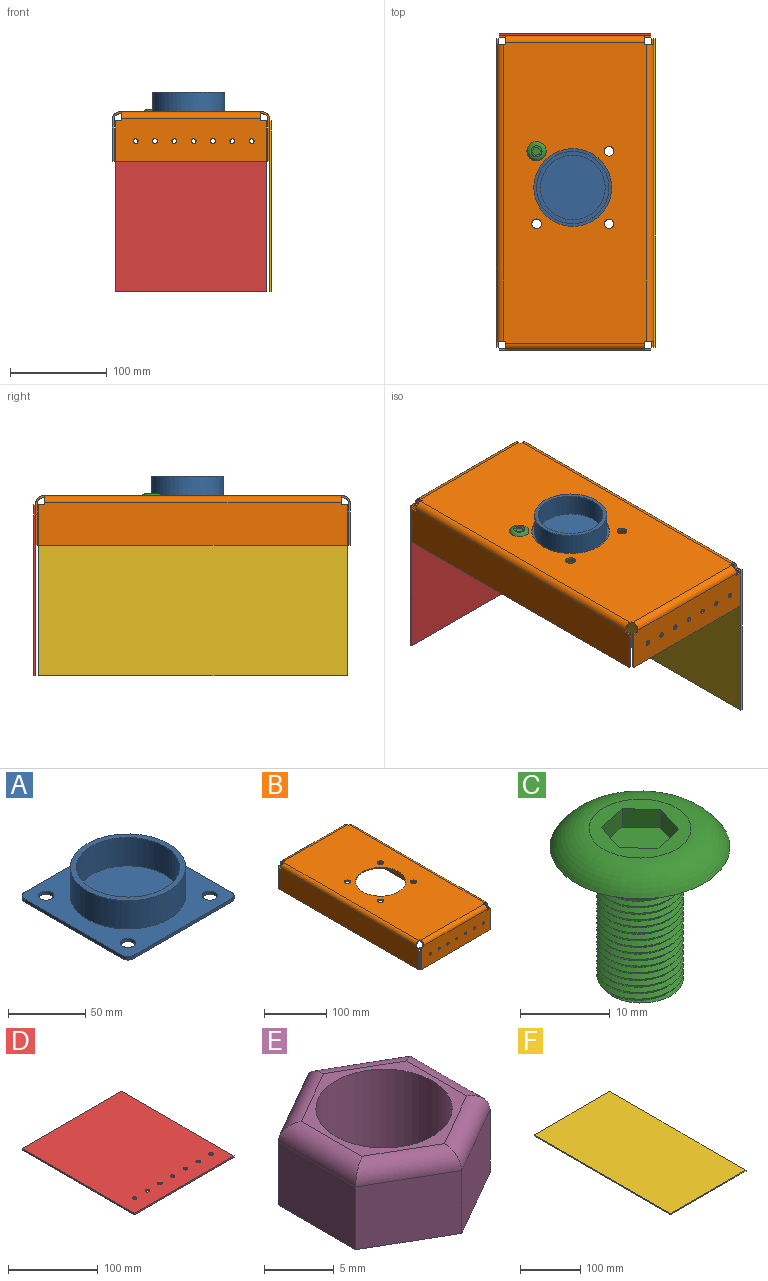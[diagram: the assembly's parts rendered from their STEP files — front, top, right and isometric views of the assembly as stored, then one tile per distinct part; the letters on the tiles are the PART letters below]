
ASSEMBLY  parts=6 mates=5
PART A: 18 faces, bbox 100x100x25 mm
  f0: plane 90x2.5mm, normal (0,1,0), area 225mm2, adj f1,f7,f8,f9
  f1: cylinder r=5mm len=5mm, axis (0,0,-1), area 19.6mm2, adj f0,f2,f8,f9
  f2: plane 90x2.5mm, normal (-1,0,0), area 225mm2, adj f1,f3,f8,f9
  f3: cylinder r=5mm len=5mm, axis (0,0,-1), area 19.6mm2, adj f2,f4,f8,f9
  f4: plane 90x2.5mm, normal (0,-1,0), area 225mm2, adj f3,f5,f8,f9
  f5: cylinder r=5mm len=5mm, axis (0,0,-1), area 19.6mm2, adj f4,f6,f8,f9
  f6: plane 90x2.5mm, normal (1,0,0), area 225mm2, adj f5,f7,f8,f9
  f7: cylinder r=5mm len=5mm, axis (0,0,-1), area 19.6mm2, adj f0,f6,f8,f9
  f8: plane 100x100mm, normal (0,0,1), area 5279.1mm2, adj f0,f1,f2,f3,f4,f5,f6,f7
  f9: plane 100x100mm, normal (0,0,-1), area 9664.4mm2, adj f0,f1,f2,f3,f4,f5,f6,f7
  f10: cylinder r=5mm len=10mm, axis (0,0,-1), area 78.5mm2, adj f8,f9
  f11: cylinder r=5mm len=10mm, axis (0,0,-1), area 78.5mm2, adj f8,f9
  f12: cylinder r=5mm len=10mm, axis (0,0,-1), area 78.5mm2, adj f8,f9
  f13: cylinder r=5mm len=10mm, axis (0,0,-1), area 78.5mm2, adj f8,f9
  f14: cylinder r=33.4mm len=66.8mm, axis (0,0,-1), area 4721.7mm2, adj f16,f17
  f15: cylinder r=37.36mm len=74.72mm, axis (0,0,-1), area 5281.8mm2, adj f8,f16
  f16: plane 74.72x74.72mm, normal (0,0,1), area 880.8mm2, adj f14,f15
  f17: plane 66.8x66.8mm, normal (0,0,1), area 3504.5mm2, adj f14
PART B: 81 faces, bbox 162.5x325x51 mm
  f0: plane 41.68x2mm, normal (-1,0,0), area 83.4mm2, adj f2,f3,f4,f5
  f1: plane 41.68x2mm, normal (1,0,0), area 83.4mm2, adj f2,f3,f4,f8
  f2: plane 156.52x44mm, normal (0,-1,0), area 6720.4mm2, adj f0,f1,f4,f5,f6,f7,f8,f65
  f3: plane 156.52x44mm, normal (0,1,0), area 6720.4mm2, adj f0,f1,f4,f5,f6,f7,f8,f66
  f4: plane 156.52x2mm, normal (0,0,-1), area 313mm2, adj f0,f1,f2,f3
  f5: plane 6.32x2mm, normal (0,0,1), area 12.6mm2, adj f0,f2,f3,f6
  f6: plane 2.32x2mm, normal (-1,0,0), area 4.6mm2, adj f2,f3,f5,f64
  f7: plane 2.32x2mm, normal (1,0,0), area 4.6mm2, adj f2,f3,f8,f63
  f8: plane 6.32x2mm, normal (0,0,1), area 12.6mm2, adj f1,f2,f3,f7
  f9: plane 311.05x148.52mm, normal (0,0,1), area 40789.9mm2, adj f11,f12,f13,f14,f15,f16,f17,f18
  f10: plane 311.05x148.52mm, normal (0,0,-1), area 40789.9mm2, adj f11,f12,f13,f14,f15,f16,f17,f18
  f11: cylinder r=4.98mm len=9.95mm, axis (0,0,1), area 62.5mm2, adj f9,f10
  f12: cylinder r=4.86mm len=9.73mm, axis (0,0,1), area 61.1mm2, adj f9,f10
  f13: cylinder r=4.98mm len=9.96mm, axis (0,0,1), area 62.6mm2, adj f9,f10
  f14: cylinder r=4.86mm len=9.72mm, axis (0,0,1), area 61.1mm2, adj f9,f10
  f15: cylinder r=40.22mm len=80.44mm, axis (0,0,1), area 505.4mm2, adj f9,f10
  f16: plane 2.32x2mm, normal (-1,0,0), area 4.6mm2, adj f9,f10,f17,f34
  f17: plane 2.32x2mm, normal (0,1,0), area 4.6mm2, adj f9,f10,f16,f46
  f18: plane 2.32x2mm, normal (0,-1,0), area 4.6mm2, adj f9,f10,f19,f47
  f19: plane 2.32x2mm, normal (-1,0,0), area 4.6mm2, adj f9,f10,f18,f64
  f20: plane 2.32x2mm, normal (1,0,0), area 4.6mm2, adj f9,f10,f21,f63
  f21: plane 2.32x2mm, normal (0,-1,0), area 4.6mm2, adj f9,f10,f20,f60
  f22: plane 2.32x2mm, normal (0,1,0), area 4.6mm2, adj f9,f10,f23,f59
  f23: plane 2.32x2mm, normal (1,0,0), area 4.6mm2, adj f9,f10,f22,f33
  f24: plane 41.68x2mm, normal (1,0,0), area 83.4mm2, adj f26,f27,f28,f29
  f25: plane 41.68x2mm, normal (-1,0,0), area 83.4mm2, adj f26,f27,f28,f32
  f26: plane 156.52x44mm, normal (0,1,0), area 6720.4mm2, adj f24,f25,f28,f29,f30,f31,f32,f35
  f27: plane 156.52x44mm, normal (0,-1,0), area 6720.4mm2, adj f24,f25,f28,f29,f30,f31,f32,f36
  f28: plane 156.52x2mm, normal (0,0,-1), area 313mm2, adj f24,f25,f26,f27
  f29: plane 6.32x2mm, normal (0,0,1), area 12.6mm2, adj f24,f26,f27,f30
  f30: plane 2.32x2mm, normal (1,0,0), area 4.6mm2, adj f26,f27,f29,f33
  f31: plane 2.32x2mm, normal (-1,0,0), area 4.6mm2, adj f26,f27,f32,f34
  f32: plane 6.32x2mm, normal (0,0,1), area 12.6mm2, adj f25,f26,f27,f31
  f33: plane 7x7mm, normal (1,0,0), area 18.8mm2, adj f23,f30,f35,f36
  f34: plane 7x7mm, normal (-1,0,0), area 18.8mm2, adj f16,f31,f35,f36
  f35: cylinder r=7mm len=143.89mm, axis (1,0,0), area 1582.2mm2, adj f9,f26,f33,f34
  f36: cylinder r=5mm len=143.89mm, axis (1,0,0), area 1130.1mm2, adj f10,f27,f33,f34
  f37: plane 41.68x2mm, normal (0,1,0), area 83.4mm2, adj f39,f40,f41,f42
  f38: plane 41.68x2mm, normal (0,-1,0), area 83.4mm2, adj f39,f40,f41,f45
  f39: plane 319.05x44mm, normal (-1,0,0), area 14008.8mm2, adj f37,f38,f41,f42,f43,f44,f45,f48
  f40: plane 319.05x44mm, normal (1,0,0), area 14008.8mm2, adj f37,f38,f41,f42,f43,f44,f45,f49
  f41: plane 319.05x2mm, normal (0,0,-1), area 638.1mm2, adj f37,f38,f39,f40
  f42: plane 6.32x2mm, normal (0,0,1), area 12.6mm2, adj f37,f39,f40,f43
  f43: plane 2.32x2mm, normal (0,1,0), area 4.6mm2, adj f39,f40,f42,f46
  f44: plane 2.32x2mm, normal (0,-1,0), area 4.6mm2, adj f39,f40,f45,f47
  f45: plane 6.32x2mm, normal (0,0,1), area 12.6mm2, adj f38,f39,f40,f44
  f46: plane 7x7mm, normal (0,1,0), area 18.8mm2, adj f17,f43,f48,f49
  f47: plane 7x7mm, normal (0,-1,0), area 18.8mm2, adj f18,f44,f48,f49
  f48: cylinder r=7mm len=306.41mm, axis (0,1,0), area 3369.2mm2, adj f9,f39,f46,f47
  f49: cylinder r=5mm len=306.41mm, axis (0,1,0), area 2406.6mm2, adj f10,f40,f46,f47
  f50: plane 41.68x2mm, normal (0,-1,0), area 83.4mm2, adj f52,f53,f54,f55
  f51: plane 41.68x2mm, normal (0,1,0), area 83.4mm2, adj f52,f53,f54,f58
  f52: plane 319.05x44mm, normal (1,0,0), area 14008.8mm2, adj f50,f51,f54,f55,f56,f57,f58,f61
  f53: plane 319.05x44mm, normal (-1,0,0), area 14008.8mm2, adj f50,f51,f54,f55,f56,f57,f58,f62
  f54: plane 319.05x2mm, normal (0,0,-1), area 638.1mm2, adj f50,f51,f52,f53
  f55: plane 6.32x2mm, normal (0,0,1), area 12.6mm2, adj f50,f52,f53,f56
  f56: plane 2.32x2mm, normal (0,-1,0), area 4.6mm2, adj f52,f53,f55,f60
  f57: plane 2.32x2mm, normal (0,1,0), area 4.6mm2, adj f52,f53,f58,f59
  f58: plane 6.32x2mm, normal (0,0,1), area 12.6mm2, adj f51,f52,f53,f57
  f59: plane 7x7mm, normal (0,1,0), area 18.8mm2, adj f22,f57,f61,f62
  f60: plane 7x7mm, normal (0,-1,0), area 18.8mm2, adj f21,f56,f61,f62
  f61: cylinder r=7mm len=306.41mm, axis (0,1,0), area 3369.2mm2, adj f9,f52,f59,f60
  f62: cylinder r=5mm len=306.41mm, axis (0,1,0), area 2406.6mm2, adj f10,f53,f59,f60
  f63: plane 7x7mm, normal (1,0,0), area 18.8mm2, adj f7,f20,f65,f66
  f64: plane 7x7mm, normal (-1,0,0), area 18.8mm2, adj f6,f19,f65,f66
  f65: cylinder r=7mm len=143.89mm, axis (1,0,0), area 1582.2mm2, adj f2,f9,f63,f64
  f66: cylinder r=5mm len=143.89mm, axis (1,0,0), area 1130.1mm2, adj f3,f10,f63,f64
  f67: cylinder r=2.5mm len=5mm, axis (0,-1,0), area 31.4mm2, adj f26,f27
  f68: cylinder r=2.5mm len=5mm, axis (0,-1,0), area 31.4mm2, adj f2,f3
  f69: cylinder r=2.5mm len=5mm, axis (0,-1,0), area 31.4mm2, adj f26,f27
  f70: cylinder r=2.5mm len=5mm, axis (0,-1,0), area 31.4mm2, adj f2,f3
  f71: cylinder r=2.5mm len=5mm, axis (0,-1,0), area 31.4mm2, adj f26,f27
  f72: cylinder r=2.5mm len=5mm, axis (0,-1,0), area 31.4mm2, adj f2,f3
  f73: cylinder r=2.5mm len=5mm, axis (0,-1,0), area 31.4mm2, adj f26,f27
  f74: cylinder r=2.5mm len=5mm, axis (0,-1,0), area 31.4mm2, adj f2,f3
  f75: cylinder r=2.5mm len=5mm, axis (0,-1,0), area 31.4mm2, adj f26,f27
  f76: cylinder r=2.5mm len=5mm, axis (0,-1,0), area 31.4mm2, adj f2,f3
  f77: cylinder r=2.5mm len=5mm, axis (0,-1,0), area 31.4mm2, adj f26,f27
  f78: cylinder r=2.5mm len=5mm, axis (0,-1,0), area 31.4mm2, adj f2,f3
  f79: cylinder r=2.5mm len=5mm, axis (0,-1,0), area 31.4mm2, adj f26,f27
  f80: cylinder r=2.5mm len=5mm, axis (0,-1,0), area 31.4mm2, adj f2,f3
PART C: 16 faces, bbox 23.5x23.5x21.4 mm
  f0: plane 11.34x11.34mm, normal (0,0,1), area 52.4mm2, adj f3,f9,f10,f11,f12,f13,f14
  f1: cylinder r=5mm len=10mm, axis (0,0,1), area 116.7mm2, adj f2,f6,f7
  f2: plane 20x20mm, normal (0,0,-1), area 235.6mm2, adj f1,f3
  f3: torus R=5.67mm, axis (0,0,-1), area 265.1mm2, adj f0,f2
  f4: bspline ~15.01x11.11mm, area 281.6mm2, adj f5,f6,f7,f8
  f5: bspline ~14.54x11.11mm, area 263mm2, adj f4,f6,f8
  f6: plane 1.12x0.59mm, normal (0,-1,0), area 0.4mm2, adj f1,f4,f5,f7
  f7: bspline ~11.55x10mm, area 9mm2, adj f1,f4,f6
  f8: plane 9.64x9.63mm, normal (0,0,-1), area 66.8mm2, adj f4,f5
  f9: plane 4.22x2.5mm, normal (-0.22,0.98,0), area 10.8mm2, adj f0,f10,f14,f15
  f10: plane 4.12x2.5mm, normal (-0.95,0.3,0), area 10.8mm2, adj f0,f9,f11,f15
  f11: plane 3.19x2.92mm, normal (-0.74,-0.67,0), area 10.8mm2, adj f0,f10,f12,f15
  f12: plane 4.22x2.5mm, normal (0.22,-0.98,0), area 10.8mm2, adj f0,f11,f13,f15
  f13: plane 4.12x2.5mm, normal (0.95,-0.3,0), area 10.8mm2, adj f0,f12,f14,f15
  f14: plane 3.19x2.92mm, normal (0.74,0.67,0), area 10.8mm2, adj f0,f9,f13,f15
  f15: plane 8.45x8.25mm, normal (0,0,1), area 48.6mm2, adj f9,f10,f11,f12,f13,f14
PART D: 13 faces, bbox 156.5x176.8x2 mm
  f0: plane 156.52x2mm, normal (0,1,0), area 313mm2, adj f1,f10,f11,f12
  f1: plane 176.78x2mm, normal (1,0,0), area 353.6mm2, adj f0,f2,f11,f12
  f2: plane 156.52x2mm, normal (0,-1,0), area 313mm2, adj f1,f10,f11,f12
  f3: cylinder r=2.5mm len=5mm, axis (0,0,1), area 31.4mm2, adj f11,f12
  f4: cylinder r=2.5mm len=5mm, axis (0,0,1), area 31.4mm2, adj f11,f12
  f5: cylinder r=2.5mm len=5mm, axis (0,0,1), area 31.4mm2, adj f11,f12
  f6: cylinder r=2.5mm len=5mm, axis (0,0,1), area 31.4mm2, adj f11,f12
  f7: cylinder r=2.5mm len=5mm, axis (0,0,1), area 31.4mm2, adj f11,f12
  f8: cylinder r=2.5mm len=5mm, axis (0,0,1), area 31.4mm2, adj f11,f12
  f9: cylinder r=2.5mm len=5mm, axis (0,0,1), area 31.4mm2, adj f11,f12
  f10: plane 176.78x2mm, normal (-1,0,0), area 353.6mm2, adj f0,f2,f11,f12
  f11: plane 176.78x156.52mm, normal (0,0,-1), area 27533.2mm2, adj f0,f1,f2,f3,f4,f5,f6,f7
  f12: plane 176.78x156.52mm, normal (0,0,1), area 27533.2mm2, adj f0,f1,f2,f3,f4,f5,f6,f7
PART E: 15 faces, bbox 13.6x15.7x7 mm
  f0: plane 6.8x5.5mm, normal (0.5,0.87,0), area 43.2mm2, adj f1,f5,f8,f12
  f1: plane 6.8x5.5mm, normal (-0.5,0.87,0), area 43.2mm2, adj f0,f2,f8,f10
  f2: plane 7.85x5.5mm, normal (-1,0,0), area 43.2mm2, adj f1,f3,f8,f9
  f3: plane 6.8x5.5mm, normal (-0.5,-0.87,0), area 43.2mm2, adj f2,f4,f8,f11
  f4: plane 6.8x5.5mm, normal (0.5,-0.87,0), area 43.2mm2, adj f3,f5,f8,f13
  f5: plane 7.85x5.5mm, normal (1,0,0), area 43.2mm2, adj f0,f4,f8,f14
  f6: cylinder r=4.87mm len=9.75mm, axis (0,0,-1), area 214.4mm2, adj f7,f8
  f7: plane 12.23x10.59mm, normal (0,0,1), area 22.5mm2, adj f6,f9,f10,f11,f12,f13,f14
  f8: plane 15.69x13.59mm, normal (0,0,-1), area 85.4mm2, adj f0,f1,f2,f3,f4,f5,f6
  f9: cylinder r=1.5mm len=7.85mm, axis (0,1,0), area 17mm2, adj f2,f7,f10,f11
  f10: cylinder r=1.5mm len=7.55mm, axis (0.87,0.5,0), area 17mm2, adj f1,f7,f9,f12
  f11: cylinder r=1.5mm len=7.55mm, axis (-0.87,0.5,0), area 17mm2, adj f3,f7,f9,f13
  f12: cylinder r=1.5mm len=7.55mm, axis (0.87,-0.5,0), area 17mm2, adj f0,f7,f10,f14
  f13: cylinder r=1.5mm len=7.55mm, axis (-0.87,-0.5,0), area 17mm2, adj f4,f7,f11,f14
  f14: cylinder r=1.5mm len=7.85mm, axis (0,-1,0), area 17mm2, adj f5,f7,f12,f13
PART F: 6 faces, bbox 176.8x319x2 mm
  f0: plane 319.05x2mm, normal (-1,0,0), area 638.1mm2, adj f1,f3,f4,f5
  f1: plane 176.78x2mm, normal (0,1,0), area 353.6mm2, adj f0,f2,f4,f5
  f2: plane 319.05x2mm, normal (1,0,0), area 638.1mm2, adj f1,f3,f4,f5
  f3: plane 176.78x2mm, normal (0,-1,0), area 353.6mm2, adj f0,f2,f4,f5
  f4: plane 319.05x176.78mm, normal (0,0,-1), area 56401.8mm2, adj f0,f1,f2,f3
  f5: plane 319.05x176.78mm, normal (0,0,1), area 56401.8mm2, adj f0,f1,f2,f3
PLACE A rot(axis=(0,0,1),180deg) t=(-84.12,73.19,47.5)mm
PLACE B at identity fixed
PLACE C t=(-71.62,76.26,52)mm
PLACE D rot(axis=(-1,0,0),90deg) t=(0,195.71,-27.35)mm
PLACE E rot(axis=(0,-1,0),180deg) t=(-71.62,76.26,47.5)mm
PLACE F rot(axis=(0,-1,0),90deg) t=(51.45,33.19,-45.71)mm
MATE pin_slot A.f12 <-> E.f6  axis (0,0,-1) through (-71.62,76.26,47.5)mm
MATE pin_slot B.f12 <-> C.f1  axis (0,0,1) through (-71.62,76.26,52)mm
MATE planar D.f6 <-> B.f67  axis (0,-1,0) through (-89.1,195.71,21.84)mm
MATE parallel B.f52 <-> F.f5  axis (1,0,0) through (49.45,-126.34,42.68)mm
MATE planar A.f14 <-> B.f15  axis (0,0,1) through (-34.12,38.76,50)mm
